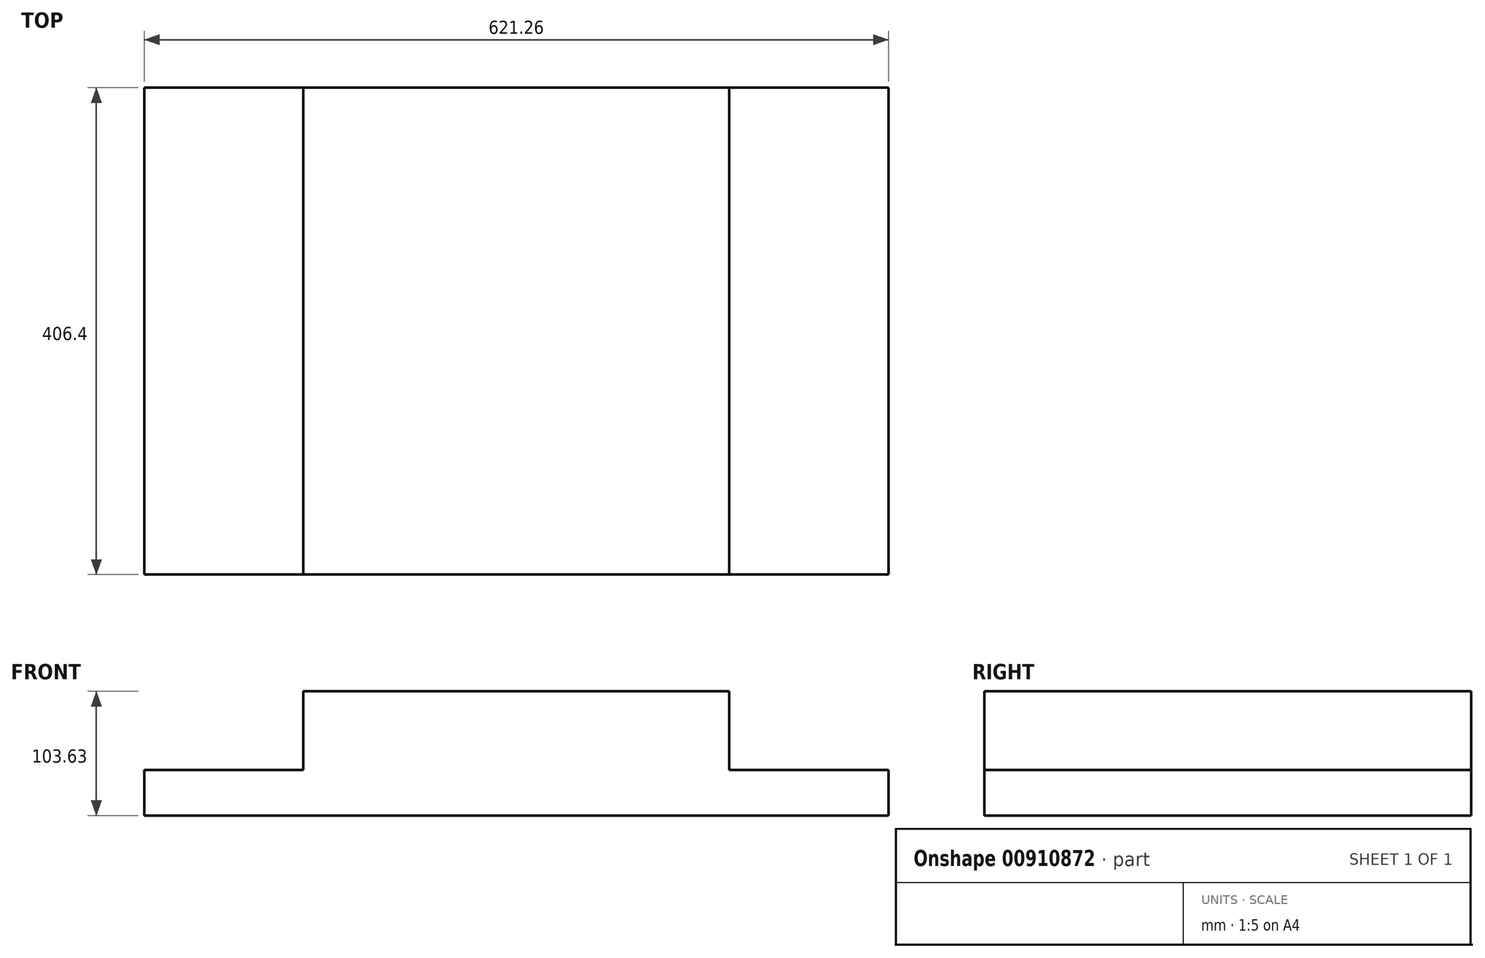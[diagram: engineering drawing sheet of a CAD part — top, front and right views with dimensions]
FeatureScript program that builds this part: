
annotation { "Feature Type Name" : "Feature", "Feature Type Description" : "" }
export const myFeature = defineFeature(function(context is Context, id is Id, definition is map)
    precondition{}
    {
        {
            var Q0;
            Q0=qCreatedBy(makeId("Front.planeOp"),FACE);
            var sketch = newSketch(context, id + "F0", { "sketchPlane" : qUnion([Q0])});
            skLineSegment(sketch, "E0.bottom", {"start": v(0, 148.05) * mm, "end": v(177.8, 148.05) * mm});
            skLineSegment(sketch, "E0.right", {"start": v(177.8, 148.05) * mm, "end": v(177.8, 82.52) * mm});
            skLineSegment(sketch, "E1.bottom", {"start": v(310.63, 44.42) * mm, "end": v(0, 44.42) * mm});
            skLineSegment(sketch, "E1.top", {"start": v(310.63, 82.52) * mm, "end": v(177.8, 82.52) * mm});
            skLineSegment(sketch, "E1.left", {"start": v(310.63, 44.42) * mm, "end": v(310.63, 82.52) * mm});
            skLineSegment(sketch, "E2", {"start": v(0, 170.19) * mm, "end": v(0, -145.28) * mm, "construction": true});
            skLineSegment(sketch, "E3.MirrorCS", {"start": v(0, 148.05) * mm, "end": v(-177.8, 148.05) * mm});
            skLineSegment(sketch, "E4.MirrorCS", {"start": v(-310.63, 44.42) * mm, "end": v(0, 44.42) * mm});
            skLineSegment(sketch, "E5.MirrorCS", {"start": v(-177.8, 148.05) * mm, "end": v(-177.8, 82.52) * mm});
            skLineSegment(sketch, "E6.MirrorCS", {"start": v(-310.63, 44.42) * mm, "end": v(-310.63, 82.52) * mm});
            skLineSegment(sketch, "E7.MirrorCS", {"start": v(-310.63, 82.52) * mm, "end": v(-177.8, 82.52) * mm});
            skSolve(sketch);
        }
        {
            var Q0;
            Q0 = qSketchRegion(id + "F0", true);
            extrude(context, id + "F1", {"entities" : qUnion([Q0]), "depth" : 406.4 * mm, "offsetDistance" : 25.4 * mm});
        }
    });
